# Revit family: Mixing_Valve-Leonard_Valve_Company-NV_150_LF
name_source: partatom
category: Pipe Accessories
revit_build: Autodesk Revit 2015 (Build: 20140606_1530(x64)
units: mm (PartAtom-declared; Revit-internal decimal feet)

## types (2) — shared parameters
BIMobject category = Valves
Brand url = http://www.leonardvalve.com
Description = The Nucleus Digitally Controlled Mixing Valve from Leonard Valve Company serves as the central monitor & control of a Domestic Hot Water System. The Nucleus Digitally Controlled Mixing Valve capabilities include:

+/- 2°F Mixed Water Temperature in accordance with ASSE 1017-2009.
+/- 2°F Mixed Water Temperature during periods of low or no system demand
0.5 GPM Minimum Flow with Continuously Operating Recirculation Pump
Automatic Shutoff of Valve upon Cold or Hot Supply Failure
System Setup & Commissioning from Nucleus Control Module–no PC or Laptop Required
LCD Display & Sensor Indicators – Set Point Temperature & Actual Temperature
BMS Interface – Native Support for Six Different Protocols including BACnet & Modbus
Ethernet Connection for PC or LAN for Valve Programming or Interrogation
Web Server to remotely monitor & control Nucleus Mixing Valve
Data Logger – stores up to 30 days of temperatures, pressure & flows
Nucleus is UL Listed & Approved to E484833. Eco-Mix Certified Lead Free Construction
Design country = United States
Edition number = 1
IFC Classification = Valve
Inlet Flow = 0.0 L/s
Manufacturer = Leonard Valve Company
Manufacturer country = United States
Manufacturer name = Leonard Valve Company
Model = NV-150-LF
OmniClass Code = 23-27 31 29
OmniClass Description = Mixing Valves
Outlet Flow = 0.0 L/s
Pipe Material = Bronze-Leonard_Valve_Company
Pipe Radius .625 = 0.6875 "
Pipe Radius .75 = 0.8125 "
Product Guid = de5db732-72ee-4206-bb4f-5ee1b4d9b55c
Product SKU = nv-150-lf
Product data url = https://bimobject.com
Product family = Mixing Valves for Liquid Services
Product group = Digitally Controlled Mixing Valves
Product url = http://www.leonardvalvecompany.com
QR code = http://bimobject.com
Technical description = http://www.leonardvalvecompany.com
UNSPSC Code = 401416
URL = http://www.leonardvalve.com
Valve Box Material = Steel-Leonard_Valve_Company-Baked_White
Weight Net (Kg) = 0
zero-valued in all types: Nominal height, Nominal width

## per-type parameters (varying)
| type | NF-150-LF-IF-RTS Double Fittings | Tee Fittings |
| NV-150-LF-IF-RTS | Yes | 7.5545 " |
| NV-150-LF BASE | No | 0.593 " |

## geometry (parser evidence)
native form markers: Blend x4, Sweep x17
no freeform markers — native parametric forms only
